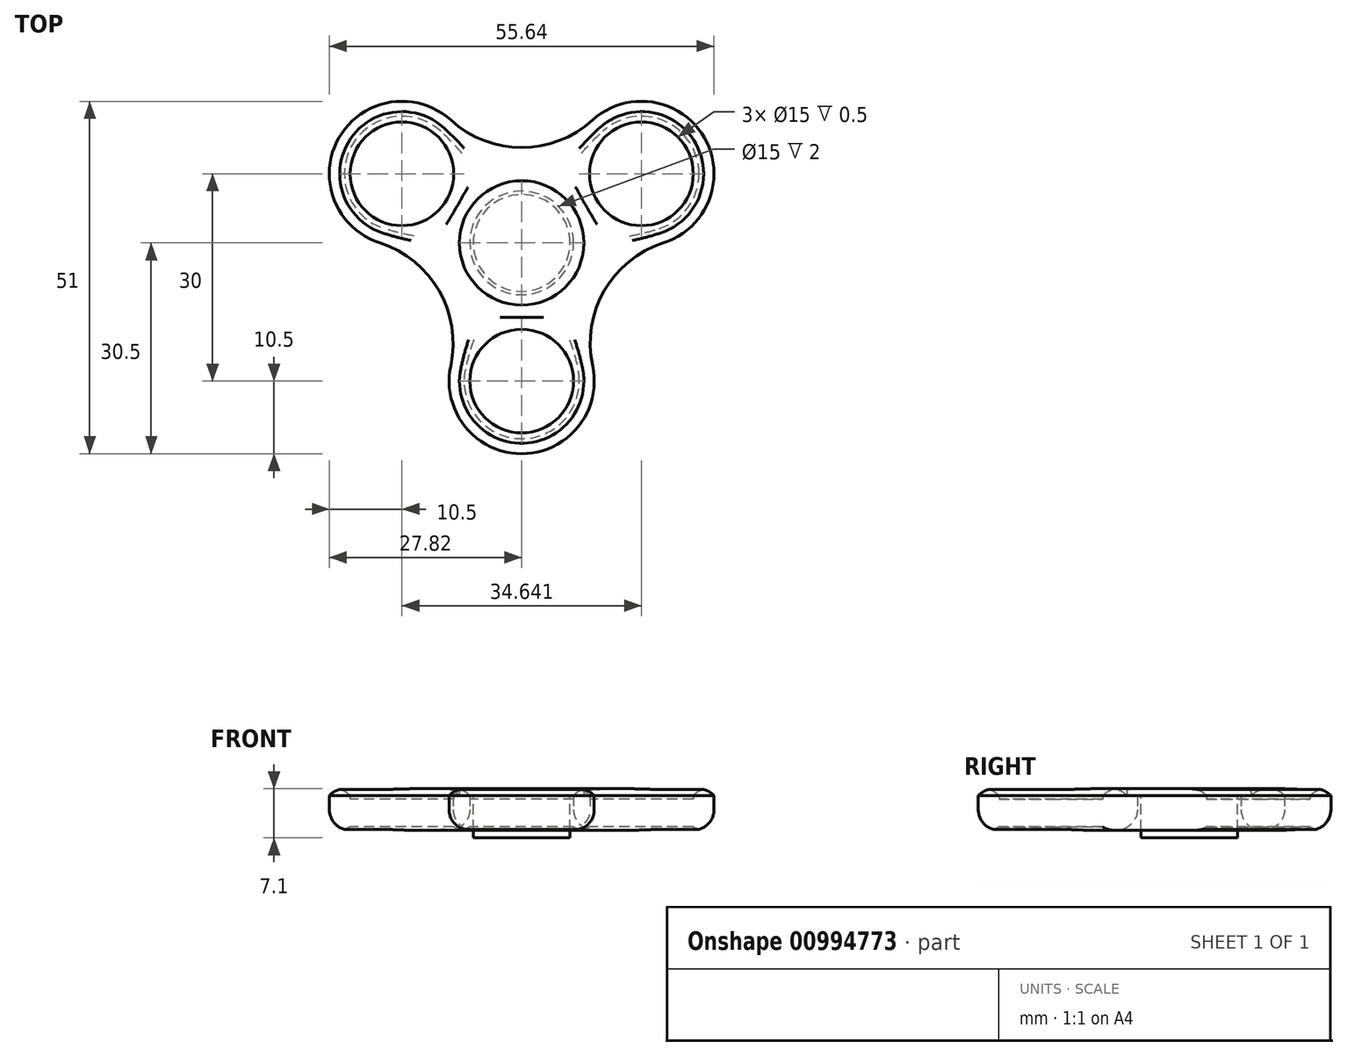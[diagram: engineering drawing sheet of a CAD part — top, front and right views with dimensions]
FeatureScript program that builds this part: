
annotation { "Feature Type Name" : "Feature", "Feature Type Description" : "" }
export const myFeature = defineFeature(function(context is Context, id is Id, definition is map)
    precondition{}
    {
        {
            var Q0;
            Q0=qCreatedBy(makeId("Top.planeOp"),FACE);
            var sketch = newSketch(context, id + "F0", { "sketchPlane" : qUnion([Q0])});
            skCircle(sketch, "E0", {"center": v(0, 0) * mm, "radius": 7.5 * mm});
            skCircle(sketch, "E1", {"center": v(0, -20) * mm, "radius": 7.5 * mm});
            skArc(sketch, "E2", {"start": v(-10.26, -17.77) * mm, "mid": v(0, -30.5) * mm, "end": v(10.26, -17.77) * mm});
            skArc(sketch, "E3.1.0", {"start": v(20.52, 0) * mm, "mid": v(26.41, 15.25) * mm, "end": v(10.26, 17.77) * mm});
            skCircle(sketch, "E3.1.1", {"center": v(17.32, 10) * mm, "radius": 7.5 * mm});
            skArc(sketch, "E3.2.0", {"start": v(-10.26, 17.77) * mm, "mid": v(-26.41, 15.25) * mm, "end": v(-20.52, 0) * mm});
            skCircle(sketch, "E3.2.1", {"center": v(-17.32, 10) * mm, "radius": 7.5 * mm});
            skArc(sketch, "E4", {"start": v(-10.26, -17.77) * mm, "mid": v(-11.96, -6.9) * mm, "end": v(-20.52, 0) * mm});
            skArc(sketch, "E5.1.0", {"start": v(20.52, 0) * mm, "mid": v(11.96, -6.9) * mm, "end": v(10.26, -17.77) * mm});
            skArc(sketch, "E5.2.0", {"start": v(-10.26, 17.77) * mm, "mid": v(0, 13.8) * mm, "end": v(10.26, 17.77) * mm});
            skSolve(sketch);
        }
        {
            var Q0;
            Q0=makeQuery(id+"F0.imprint","IMPRINT",FACE,{"disambiguationData":[TD([[makeQuery(id+"F0.imprint","IMPRINT",EDGE,{"derivedFrom":sQuery(id+"F0.wireOp",EDGE,"E0")}),-1.0]])]});
            extrude(context, id + "F1", {"entities" : qUnion([Q0]), "endBound" : BoundingType.SYMMETRIC, "depth" : 5 * mm, "offsetDistance" : 25 * mm});
        }
        {
            var Q0;
            Q0=makeQuery(id+"F0.imprint","IMPRINT",FACE,{"disambiguationData":[TD([[makeQuery(id+"F0.imprint","IMPRINT",EDGE,{"derivedFrom":sQuery(id+"F0.wireOp",EDGE,"E3.2.1")}),1.0]])]});
            var Q1;
            Q1=makeQuery(id+"F0.imprint","IMPRINT",FACE,{"disambiguationData":[TD([[makeQuery(id+"F0.imprint","IMPRINT",EDGE,{"derivedFrom":sQuery(id+"F0.wireOp",EDGE,"E3.1.1")}),1.0]])]});
            var Q2;
            Q2=makeQuery(id+"F0.imprint","IMPRINT",FACE,{"disambiguationData":[TD([[makeQuery(id+"F0.imprint","IMPRINT",EDGE,{"derivedFrom":sQuery(id+"F0.wireOp",EDGE,"E1")}),1.0]])]});
            extrude(context, id + "F2", {"entities" : qUnion([Q0, Q1, Q2]), "operationType" : NewBodyOperationType.ADD, "endBound" : BoundingType.SYMMETRIC, "depth" : 4 * mm, "offsetDistance" : 25 * mm});
        }
        {
            var Q0;
            Q0=makeQuery(id+"F1.opExtrude","CAP_FACE",FACE,{"disambiguationData":[OSD([sQuery(id+"F0.wireOp",EDGE,"E0"),sQuery(id+"F0.wireOp",EDGE,"E1"),sQuery(id+"F0.wireOp",EDGE,"E2"),sQuery(id+"F0.wireOp",EDGE,"E3.1.0"),sQuery(id+"F0.wireOp",EDGE,"E3.1.1"),sQuery(id+"F0.wireOp",EDGE,"E3.2.0"),sQuery(id+"F0.wireOp",EDGE,"E3.2.1"),sQuery(id+"F0.wireOp",EDGE,"E4"),sQuery(id+"F0.wireOp",EDGE,"E5.1.0"),sQuery(id+"F0.wireOp",EDGE,"E5.2.0")])],"isStart":false});
            var sketch = newSketch(context, id + "F3", { "sketchPlane" : qUnion([Q0])});
            skCircle(sketch, "E6.0", {"center": v(0, 0) * mm, "radius": 7 * mm});
            skCircle(sketch, "E7", {"center": v(0, 0) * mm, "radius": 3 * mm});
            skCircle(sketch, "E8.0", {"center": v(0, 0) * mm, "radius": 9 * mm});
            skSolve(sketch);
        }
        {
            var Q0;
            Q0=makeQuery(id+"F3.imprint","IMPRINT",FACE,{"disambiguationData":[TD([[makeQuery(id+"F3.imprint","IMPRINT",EDGE,{"derivedFrom":sQuery(id+"F3.wireOp",EDGE,"E6.0")}),1.0]])]});
            extrude(context, id + "F4", {"entities" : qUnion([Q0]), "oppositeDirection" : true, "depth" : 5.1 * mm, "offsetDistance" : 25 * mm});
        }
        {
            var Q0;
            Q0=makeQuery(id+"F3.imprint","IMPRINT",FACE,{"disambiguationData":[TD([[makeQuery(id+"F3.imprint","IMPRINT",EDGE,{"derivedFrom":sQuery(id+"F3.wireOp",EDGE,"E8.0")}),1.0]])]});
            var Q1;
            Q1=makeQuery(id+"F3.imprint","IMPRINT",FACE,{"disambiguationData":[TD([[makeQuery(id+"F3.imprint","IMPRINT",EDGE,{"derivedFrom":sQuery(id+"F3.wireOp",EDGE,"E6.0")}),1.0]])]});
            var Q2;
            Q2=makeQuery(id+"F3.imprint","IMPRINT",FACE,{"disambiguationData":[TD([[makeQuery(id+"F3.imprint","IMPRINT",EDGE,{"derivedFrom":sQuery(id+"F3.wireOp",EDGE,"E6.0")}),-1.0]])]});
            var Q3;
            Q3=makeQuery(id+"F3.imprint","IMPRINT",FACE,{"disambiguationData":[TD([[makeQuery(id+"F3.imprint","IMPRINT",EDGE,{"derivedFrom":sQuery(id+"F3.wireOp",EDGE,"E7")}),1.0]])]});
            var Q4;
            Q4=sQuery(id+"F3.wireOp",EDGE,"E8.0");
            extrude(context, id + "F5", {"entities" : qUnion([Q0, Q1, Q2, Q3]), "operationType" : NewBodyOperationType.ADD, "surfaceEntities" : qUnion([Q4]), "depth" : 1 * mm, "offsetDistance" : 25 * mm});
        }
        {
            var Q0;
            Q0=makeQuery(id+"F4.opExtrude","CAP_FACE",FACE,{"disambiguationData":[OSD([sQuery(id+"F3.wireOp",EDGE,"E6.0"),sQuery(id+"F3.wireOp",EDGE,"E7")])],"isStart":false});
            var sketch = newSketch(context, id + "F6", { "sketchPlane" : qUnion([Q0])});
            skCircle(sketch, "E9.0", {"center": v(0, 0) * mm, "radius": 3.1 * mm});
            skCircle(sketch, "E10.0", {"center": v(0, 0) * mm, "radius": 9 * mm});
            skSolve(sketch);
        }
        {
            var Q0;
            Q0=makeQuery(id+"F6.imprint","IMPRINT",FACE,{"disambiguationData":[TD([[makeQuery(id+"F6.imprint","IMPRINT",EDGE,{"derivedFrom":makeQuery(id+"F4.opExtrude","CAP_EDGE",EDGE,{"disambiguationData":[OSD([sQuery(id+"F3.wireOp",EDGE,"E7")])],"isStart":false})}),-1.0]])]});
            var Q1;
            Q1=makeQuery(id+"F3.imprint","IMPRINT",FACE,{"disambiguationData":[TD([[makeQuery(id+"F3.imprint","IMPRINT",EDGE,{"derivedFrom":sQuery(id+"F3.wireOp",EDGE,"E8.0")}),-1.0]])]});
            var Q2;
            Q2=makeQuery(id+"F5.opExtrude","CAP_FACE",FACE,{"disambiguationData":[OSD([sQuery(id+"F3.wireOp",EDGE,"E8.0")])],"isStart":false});
            extrude(context, id + "F7", {"entities" : qUnion([Q0, Q1]), "endBound" : BoundingType.UP_TO_SURFACE, "oppositeDirection" : true, "depth" : 25 * mm, "endBoundEntityFace" : qUnion([Q2]), "offsetDistance" : 25 * mm});
        }
        {
            var Q0;
            Q0=makeQuery(id+"F6.imprint","IMPRINT",FACE,{"disambiguationData":[TD([[makeQuery(id+"F6.imprint","IMPRINT",EDGE,{"derivedFrom":sQuery(id+"F6.wireOp",EDGE,"E9.0")}),1.0]])]});
            var Q1;
            Q1=makeQuery(id+"F6.imprint","IMPRINT",FACE,{"disambiguationData":[TD([[makeQuery(id+"F6.imprint","IMPRINT",EDGE,{"derivedFrom":sQuery(id+"F6.wireOp",EDGE,"E10.0")}),-1.0]])]});
            var Q2;
            Q2=makeQuery(id+"F6.imprint","IMPRINT",FACE,{"disambiguationData":[TD([[makeQuery(id+"F6.imprint","IMPRINT",EDGE,{"derivedFrom":makeQuery(id+"F4.opExtrude","CAP_EDGE",EDGE,{"disambiguationData":[OSD([sQuery(id+"F3.wireOp",EDGE,"E7")])],"isStart":false})}),-1.0]])]});
            var Q3;
            Q3=makeQuery(id+"F6.imprint","IMPRINT",FACE,{"disambiguationData":[TD([[makeQuery(id+"F6.imprint","IMPRINT",EDGE,{"derivedFrom":sQuery(id+"F6.wireOp",EDGE,"E9.0")}),-1.0]])]});
            extrude(context, id + "F8", {"entities" : qUnion([Q0, Q1, Q2, Q3]), "operationType" : NewBodyOperationType.ADD, "depth" : 1 * mm, "offsetDistance" : 25 * mm});
        }
        {
            var Q0;
            Q0=makeQuery(id+"F1.opExtrude","CAP_FACE",FACE,{"disambiguationData":[OSD([sQuery(id+"F0.wireOp",EDGE,"E0"),sQuery(id+"F0.wireOp",EDGE,"E1"),sQuery(id+"F0.wireOp",EDGE,"E2"),sQuery(id+"F0.wireOp",EDGE,"E3.1.0"),sQuery(id+"F0.wireOp",EDGE,"E3.1.1"),sQuery(id+"F0.wireOp",EDGE,"E3.2.0"),sQuery(id+"F0.wireOp",EDGE,"E3.2.1"),sQuery(id+"F0.wireOp",EDGE,"E4"),sQuery(id+"F0.wireOp",EDGE,"E5.1.0"),sQuery(id+"F0.wireOp",EDGE,"E5.2.0")])],"isStart":true});
            var Q1;
            Q1=makeQuery(id+"F7.opExtrude","CAP_FACE",FACE,{"disambiguationData":[OSD([sQuery(id+"F0.wireOp",EDGE,"E1"),sQuery(id+"F0.wireOp",EDGE,"E2"),sQuery(id+"F0.wireOp",EDGE,"E3.1.0"),sQuery(id+"F0.wireOp",EDGE,"E3.1.1"),sQuery(id+"F0.wireOp",EDGE,"E3.2.0"),sQuery(id+"F0.wireOp",EDGE,"E3.2.1"),sQuery(id+"F0.wireOp",EDGE,"E4"),sQuery(id+"F0.wireOp",EDGE,"E5.1.0"),sQuery(id+"F0.wireOp",EDGE,"E5.2.0"),sQuery(id+"F3.wireOp",EDGE,"E8.0")])],"isStart":false});
            fillet(context, id + "F9", {"entities" : qUnion([Q0, Q1]), "radius" : 3 * mm, "tangentPropagation" : true, "allowEdgeOverflow" : false});
        }
        {
            var Q0;
            Q0=makeQuery(id+"F8.opExtrude","CAP_FACE",FACE,{"disambiguationData":[OSD([sQuery(id+"F6.wireOp",EDGE,"E10.0")])],"isStart":false});
            var Q1;
            Q1=makeQuery(id+"F5.opExtrude","CAP_EDGE",EDGE,{"disambiguationData":[OSD([sQuery(id+"F3.wireOp",EDGE,"E8.0")])],"isStart":false});
            fillet(context, id + "F10", {"entities" : qUnion([Q0, Q1]), "radius" : 0.5 * mm, "tangentPropagation" : true, "allowEdgeOverflow" : false});
        }
    });
